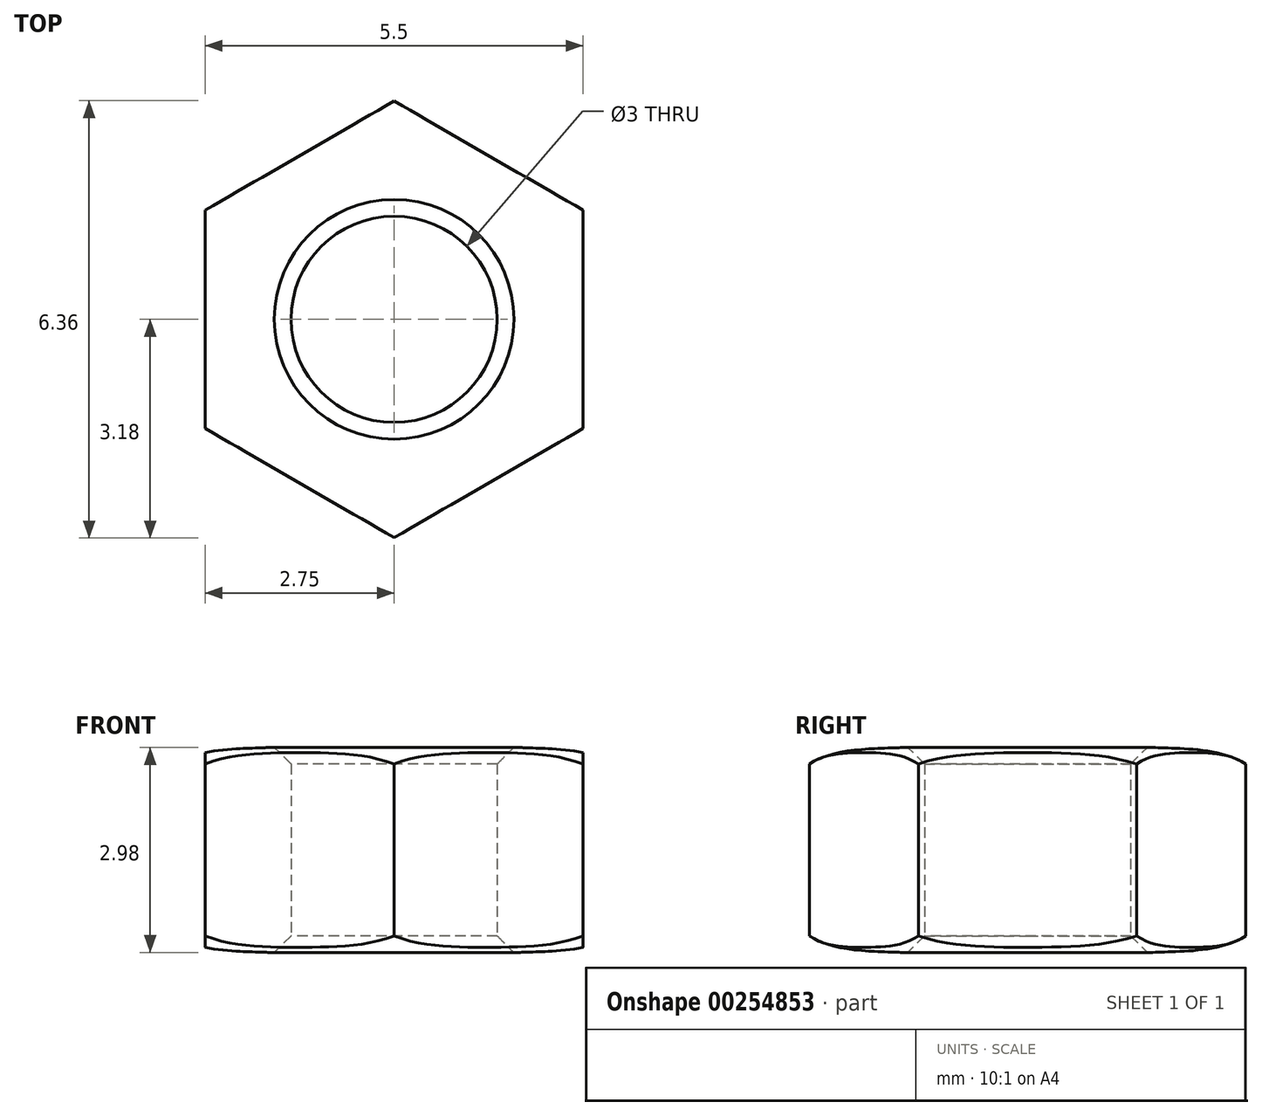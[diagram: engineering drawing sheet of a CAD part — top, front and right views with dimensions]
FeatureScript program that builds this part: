
annotation { "Feature Type Name" : "Feature", "Feature Type Description" : "" }
export const myFeature = defineFeature(function(context is Context, id is Id, definition is map)
    precondition{}
    {
        {
            var Q0;
            Q0=qCreatedBy(makeId("Top.planeOp"),FACE);
            var sketch = newSketch(context, id + "F0", { "sketchPlane" : qUnion([Q0])});
            skCircle(sketch, "E0.cCircle", {"center": v(0, 0) * mm, "radius": 2.75 * mm, "construction": true});
            skLineSegment(sketch, "E0.0", {"start": v(2.75, 1.59) * mm, "end": v(2.75, -1.59) * mm});
            skLineSegment(sketch, "E0.1", {"start": v(2.75, -1.59) * mm, "end": v(0, -3.18) * mm});
            skLineSegment(sketch, "E0.2", {"start": v(0, -3.18) * mm, "end": v(-2.75, -1.59) * mm});
            skLineSegment(sketch, "E0.3", {"start": v(-2.75, -1.59) * mm, "end": v(-2.75, 1.59) * mm});
            skLineSegment(sketch, "E0.4", {"start": v(-2.75, 1.59) * mm, "end": v(0, 3.18) * mm});
            skLineSegment(sketch, "E0.5", {"start": v(0, 3.18) * mm, "end": v(2.75, 1.59) * mm});
            skPoint(sketch, "E0.0.midPoint", {"position": v(2.75, 0) * mm});
            skCircle(sketch, "E1", {"center": v(0, 0) * mm, "radius": 1.5 * mm});
            skSolve(sketch);
        }
        {
            var Q0;
            Q0 = qSketchRegion(id + "F0", true);
            extrude(context, id + "F1", {"entities" : qUnion([Q0]), "depth" : 3 * mm, "symmetric" : true});
        }
        {
            var Q0;
            Q0=makeQuery(id+"F1.opExtrude","CAP_EDGE",EDGE,{"disambiguationData":[OSD([sQuery(id+"F0.wireOp",EDGE,"E1")])],"isStart":false});
            chamfer(context, id + "F2", {"entities" : qUnion([Q0]), "width" : 0.25 * mm, "tangentPropagation" : true});
        }
        {
            var Q0;
            Q0=makeQuery(id+"F1.opExtrude","CAP_EDGE",EDGE,{"disambiguationData":[OSD([sQuery(id+"F0.wireOp",EDGE,"E1")])],"isStart":true});
            chamfer(context, id + "F3", {"entities" : qUnion([Q0]), "width" : 0.25 * mm, "tangentPropagation" : true});
        }
        {
            var Q0;
            Q0=qCreatedBy(makeId("Right.planeOp"),FACE);
            var sketch = newSketch(context, id + "F4", { "sketchPlane" : qUnion([Q0])});
            skFitSpline(sketch, "E2", {"points": [v(0, 1.5) * mm, v(2, 1.48) * mm, v(3.47, 0.9) * mm], "startDerivative": vector(8.87, 0.07) * mm, "endDerivative": vector(1.26, -3.57) * mm});
            skFitSpline(sketch, "E3.MirrorCS", {"points": [v(0, -1.5) * mm, v(2, -1.48) * mm, v(3.47, -0.9) * mm], "startDerivative": vector(8.87, -0.07) * mm, "endDerivative": vector(1.26, 3.57) * mm});
            skLineSegment(sketch, "E4", {"start": v(3.47, 0.9) * mm, "end": v(3.47, -0.9) * mm});
            skLineSegment(sketch, "E5", {"start": v(0, 1.5) * mm, "end": v(0, 1.9) * mm});
            skLineSegment(sketch, "E6", {"start": v(0, 1.9) * mm, "end": v(4.12, 1.9) * mm});
            skLineSegment(sketch, "E7", {"start": v(4.12, 1.9) * mm, "end": v(4.12, -1.85) * mm});
            skLineSegment(sketch, "E8", {"start": v(4.12, -1.85) * mm, "end": v(0, -1.85) * mm});
            skLineSegment(sketch, "E9", {"start": v(0, -1.85) * mm, "end": v(0, -1.5) * mm});
            skSolve(sketch);
        }
        {
            var Q0;
            Q0 = qSketchRegion(id + "F4", true);
            var Q1;
            Q1=makeQuery(id+"F1.opExtrude","SWEPT_FACE",FACE,{"disambiguationData":[OSD([sQuery(id+"F0.wireOp",EDGE,"E1")])]});
            revolve(context, id + "F5", {"operationType" : NewBodyOperationType.REMOVE, "entities" : qUnion([Q0]), "axis" : qUnion([Q1]), "revolveType" : RevolveType.FULL, "oppositeDirection" : true});
        }
    });
